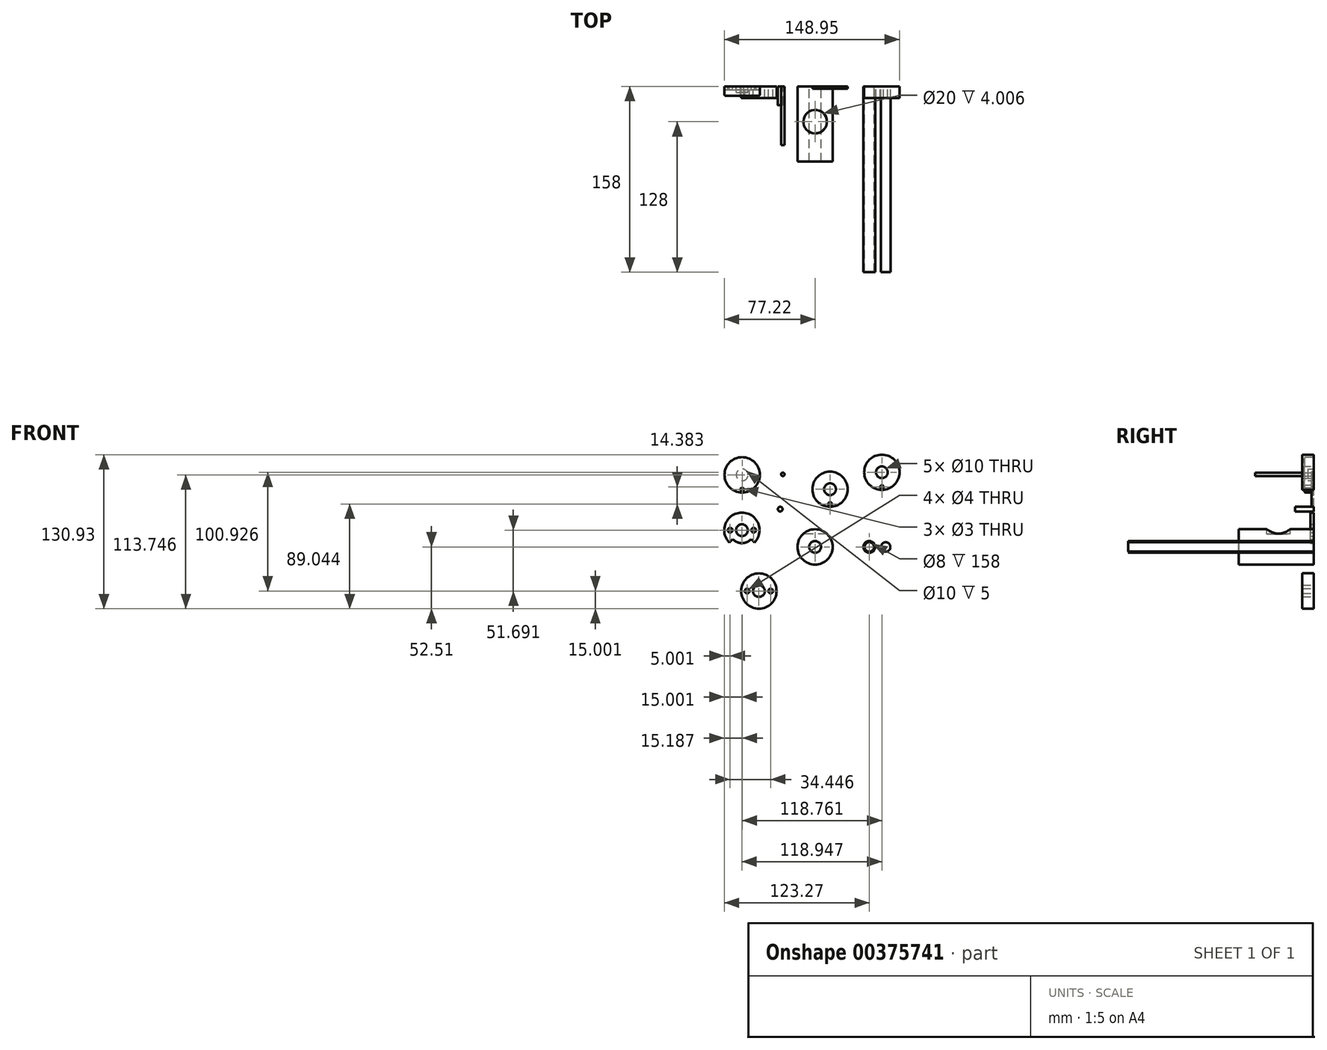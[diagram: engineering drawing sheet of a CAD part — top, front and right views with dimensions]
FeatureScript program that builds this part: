
annotation { "Feature Type Name" : "Feature", "Feature Type Description" : "" }
export const myFeature = defineFeature(function(context is Context, id is Id, definition is map)
    precondition{}
    {
        {
            var Q0;
            Q0=qCreatedBy(makeId("Front.planeOp"),FACE);
            var sketch = newSketch(context, id + "F0", { "sketchPlane" : qUnion([Q0])});
            skCircle(sketch, "E0", {"center": v(0, 0) * mm, "radius": 15 * mm});
            skCircle(sketch, "E1", {"center": v(0, 0) * mm, "radius": 5 * mm});
            skSolve(sketch);
        }
        {
            var Q0;
            Q0 = qSketchRegion(id + "F0", true);
            extrude(context, id + "F1", {"entities" : qUnion([Q0]), "depth" : 64 * mm});
        }
        {
            var Q0;
            Q0=qCreatedBy(makeId("Front.planeOp"),FACE);
            var sketch = newSketch(context, id + "F2", { "sketchPlane" : qUnion([Q0])});
            skArc(sketch, "E2", {"start": v(-51.43, 3.76) * mm, "mid": v(-62.22, 29.18) * mm, "end": v(-73, 3.76) * mm});
            skCircle(sketch, "E3", {"center": v(-62.22, 14.18) * mm, "radius": 5 * mm});
            skCircle(sketch, "E4", {"center": v(-72.22, 14.18) * mm, "radius": 2 * mm});
            skCircle(sketch, "E5", {"center": v(-52.22, 14.18) * mm, "radius": 2 * mm});
            skLineSegment(sketch, "E6", {"start": v(-54.3, 6.54) * mm, "end": v(-51.43, 3.76) * mm});
            skLineSegment(sketch, "E7", {"start": v(-70.13, 6.54) * mm, "end": v(-73, 3.76) * mm});
            skArc(sketch, "E8", {"start": v(-70.13, 6.54) * mm, "mid": v(-62.22, 3.18) * mm, "end": v(-54.3, 6.54) * mm});
            skLineSegment(sketch, "E9", {"start": v(-62.22, 14.18) * mm, "end": v(-47.22, 14.18) * mm});
            skSolve(sketch);
        }
        {
            var Q0;
            Q0 = qSketchRegion(id + "F2", true);
            extrude(context, id + "F3", {"entities" : qUnion([Q0]), "depth" : 3 * mm});
        }
        {
            var Q0;
            Q0=qCreatedBy(makeId("Front.planeOp"),FACE);
            var sketch = newSketch(context, id + "F4", { "sketchPlane" : qUnion([Q0])});
            skCircle(sketch, "E10", {"center": v(-47.77, -37.5) * mm, "radius": 15 * mm});
            skCircle(sketch, "E11", {"center": v(-47.77, -37.5) * mm, "radius": 5 * mm});
            skCircle(sketch, "E12", {"center": v(-57.77, -37.5) * mm, "radius": 2 * mm});
            skCircle(sketch, "E13", {"center": v(-37.77, -37.5) * mm, "radius": 2 * mm});
            skSolve(sketch);
        }
        {
            var Q0;
            Q0 = qSketchRegion(id + "F4", true);
            extrude(context, id + "F5", {"entities" : qUnion([Q0]), "depth" : 10 * mm});
        }
        {
            var Q0;
            Q0=qCreatedBy(makeId("Front.planeOp"),FACE);
            var sketch = newSketch(context, id + "F6", { "sketchPlane" : qUnion([Q0])});
            skCircle(sketch, "E14", {"center": v(12.7, 49.03) * mm, "radius": 15 * mm});
            skCircle(sketch, "E15", {"center": v(12.7, 49.03) * mm, "radius": 5 * mm});
            skCircle(sketch, "E16", {"center": v(12.7, 36.53) * mm, "radius": 1.5 * mm});
            skSolve(sketch);
        }
        {
            var Q0;
            Q0 = qSketchRegion(id + "F6", true);
            extrude(context, id + "F7", {"entities" : qUnion([Q0]), "depth" : 2 * mm});
        }
        {
            var Q0;
            Q0=qCreatedBy(makeId("Top.planeOp"),FACE);
            cPlane(context, id + "F8", {"entities" : qUnion([Q0]), "cplaneType" : CPlaneType.OFFSET, "offset" : 15 * mm, "width" : 150 * mm, "height" : 150 * mm});
        }
        {
            var Q0;
            Q0=qCreatedBy(id+"F8.planeOp",FACE);
            var sketch = newSketch(context, id + "F9", { "sketchPlane" : qUnion([Q0])});
            skCircle(sketch, "E17", {"center": v(0, -30) * mm, "radius": 10 * mm});
            skSolve(sketch);
        }
        {
            var Q0;
            Q0 = qSketchRegion(id + "F9", true);
            extrude(context, id + "F10", {"entities" : qUnion([Q0]), "operationType" : NewBodyOperationType.REMOVE, "oppositeDirection" : true, "depth" : 4 * mm});
        }
        {
            var Q0;
            Q0=qCreatedBy(makeId("Front.planeOp"),FACE);
            var sketch = newSketch(context, id + "F11", { "sketchPlane" : qUnion([Q0])});
            skCircle(sketch, "E18", {"center": v(46.05, 0) * mm, "radius": 5 * mm});
            skCircle(sketch, "E19", {"center": v(46.05, 0) * mm, "radius": 4 * mm});
            skSolve(sketch);
        }
        {
            var Q0;
            Q0 = qSketchRegion(id + "F11", true);
            extrude(context, id + "F12", {"entities" : qUnion([Q0]), "depth" : 158 * mm});
        }
        {
            var Q0;
            Q0=qCreatedBy(makeId("Front.planeOp"),FACE);
            var sketch = newSketch(context, id + "F13", { "sketchPlane" : qUnion([Q0])});
            skCircle(sketch, "E20", {"center": v(60, 0) * mm, "radius": 4 * mm});
            skSolve(sketch);
        }
        {
            var Q0;
            Q0 = qSketchRegion(id + "F13", true);
            var Q1;
            Q1 = qSketchRegion(id + "F15", true);
            extrude(context, id + "F14", {"entities" : qUnion([Q0, Q1]), "depth" : 158 * mm});
        }
        {
            var Q0;
            Q0=qCreatedBy(makeId("Front.planeOp"),FACE);
            var sketch = newSketch(context, id + "F15", { "sketchPlane" : qUnion([Q0])});
            skCircle(sketch, "E21", {"center": v(-29.66, 32.1) * mm, "radius": 2 * mm});
            skSolve(sketch);
        }
        {
            var Q0;
            Q0 = qSketchRegion(id + "F15", true);
            extrude(context, id + "F16", {"entities" : qUnion([Q0]), "depth" : 16 * mm});
        }
        {
            var Q0;
            Q0=qCreatedBy(makeId("Front.planeOp"),FACE);
            var sketch = newSketch(context, id + "F17", { "sketchPlane" : qUnion([Q0])});
            skCircle(sketch, "E22", {"center": v(-62.03, 61.24) * mm, "radius": 15 * mm});
            skCircle(sketch, "E23", {"center": v(-62.03, 48.74) * mm, "radius": 1.5 * mm});
            skCircle(sketch, "E24", {"center": v(56.73, 63.42) * mm, "radius": 15 * mm});
            skCircle(sketch, "E25", {"center": v(56.73, 50.92) * mm, "radius": 1.5 * mm});
            skCircle(sketch, "E26", {"center": v(56.73, 63.42) * mm, "radius": 5 * mm});
            skSolve(sketch);
        }
        {
            var Q0;
            Q0=makeQuery(id+"F17.imprint","IMPRINT",FACE,{"disambiguationData":[TD([[makeQuery(id+"F17.imprint","IMPRINT",EDGE,{"derivedFrom":sQuery(id+"F17.wireOp",EDGE,"E22")}),1.0]])]});
            extrude(context, id + "F18", {"entities" : qUnion([Q0]), "depth" : 8 * mm});
        }
        {
            var Q0;
            Q0=qCreatedBy(makeId("Front.planeOp"),FACE);
            var sketch = newSketch(context, id + "F19", { "sketchPlane" : qUnion([Q0])});
            skCircle(sketch, "E27", {"center": v(-27.45, 61.7) * mm, "radius": 1.5 * mm});
            skSolve(sketch);
        }
        {
            var Q0;
            Q0 = qSketchRegion(id + "F19", true);
            extrude(context, id + "F20", {"entities" : qUnion([Q0]), "depth" : 50 * mm});
        }
        {
            var Q0;
            Q0=makeQuery(id+"F18.opExtrude","CAP_EDGE",EDGE,{"disambiguationData":[OSD([sQuery(id+"F17.wireOp",EDGE,"E22")])],"isStart":false});
            fillet(context, id + "F21", {"entities" : qUnion([Q0]), "radius" : 1 * mm, "tangentPropagation" : true, "allowEdgeOverflow" : false});
        }
        {
            var Q0;
            Q0=makeQuery(id+"F17.imprint","IMPRINT",FACE,{"disambiguationData":[TD([[makeQuery(id+"F17.imprint","IMPRINT",EDGE,{"derivedFrom":sQuery(id+"F17.wireOp",EDGE,"E24")}),1.0]])]});
            extrude(context, id + "F22", {"entities" : qUnion([Q0]), "depth" : 10 * mm});
        }
        {
            var Q0;
            Q0=makeQuery(id+"F18.opExtrude","CAP_FACE",FACE,{"disambiguationData":[OSD([sQuery(id+"F17.wireOp",EDGE,"E22"),sQuery(id+"F17.wireOp",EDGE,"E23")])],"isStart":true});
            var sketch = newSketch(context, id + "F23", { "sketchPlane" : qUnion([Q0])});
            skCircle(sketch, "E28", {"center": v(62.03, 61.24) * mm, "radius": 5 * mm});
            skSolve(sketch);
        }
        {
            var Q0;
            Q0 = qSketchRegion(id + "F23", true);
            extrude(context, id + "F24", {"entities" : qUnion([Q0]), "operationType" : NewBodyOperationType.REMOVE, "oppositeDirection" : true, "depth" : 5 * mm});
        }
    });
